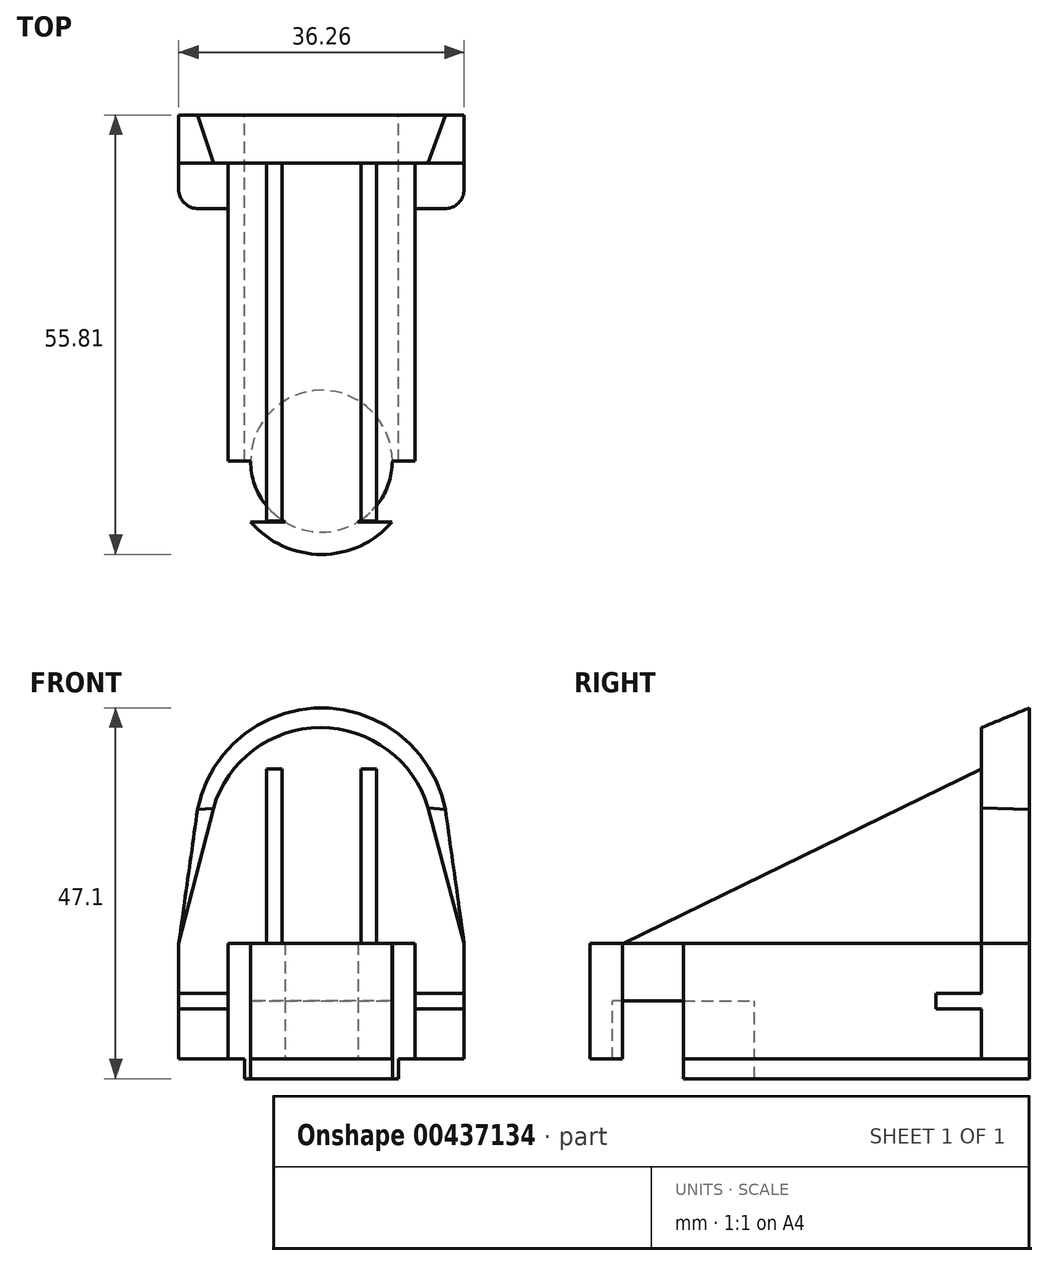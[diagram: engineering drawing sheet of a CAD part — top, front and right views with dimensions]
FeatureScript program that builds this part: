
annotation { "Feature Type Name" : "Feature", "Feature Type Description" : "" }
export const myFeature = defineFeature(function(context is Context, id is Id, definition is map)
    precondition{}
    {
        {
            var Q0;
            Q0=qCreatedBy(makeId("Front.planeOp"),FACE);
            var sketch = newSketch(context, id + "F0", { "sketchPlane" : qUnion([Q0])});
            skLineSegment(sketch, "E0.bottom", {"start": v(-18.13, 7.35) * mm, "end": v(18.13, 7.35) * mm});
            skLineSegment(sketch, "E0.top", {"start": v(-18.13, -7.35) * mm, "end": v(18.13, -7.35) * mm});
            skLineSegment(sketch, "E0.left", {"start": v(-18.13, 7.35) * mm, "end": v(-18.13, -7.35) * mm});
            skLineSegment(sketch, "E0.right", {"start": v(18.13, 7.35) * mm, "end": v(18.13, -7.35) * mm});
            skPoint(sketch, "E0.middle", {"position": v(0, 0) * mm});
            skLineSegment(sketch, "E1.bottom", {"start": v(-9.78, 7.35) * mm, "end": v(9.78, 7.35) * mm});
            skLineSegment(sketch, "E1.top", {"start": v(-9.78, -9.85) * mm, "end": v(9.78, -9.85) * mm});
            skLineSegment(sketch, "E1.left", {"start": v(-9.78, 7.35) * mm, "end": v(-9.78, -9.85) * mm});
            skLineSegment(sketch, "E1.right", {"start": v(9.78, 7.35) * mm, "end": v(9.78, -9.85) * mm});
            skPoint(sketch, "E1.middle", {"position": v(0, -1.25) * mm});
            skLineSegment(sketch, "E2.bottom", {"start": v(-11.87, 7.35) * mm, "end": v(11.87, 7.35) * mm});
            skLineSegment(sketch, "E2.top", {"start": v(-11.87, -7.35) * mm, "end": v(11.87, -7.35) * mm});
            skLineSegment(sketch, "E2.left", {"start": v(-11.87, 7.35) * mm, "end": v(-11.87, -7.35) * mm});
            skLineSegment(sketch, "E2.right", {"start": v(11.87, 7.35) * mm, "end": v(11.87, -7.35) * mm});
            skLineSegment(sketch, "E3", {"start": v(0, -9.85) * mm, "end": v(0, 37.25) * mm, "construction": true});
            skPoint(sketch, "E3.endSnap0", {"position": v(0, 7.35) * mm});
            skLineSegment(sketch, "E4", {"start": v(-18.13, 7.35) * mm, "end": v(-15.74, 24.38) * mm});
            skLineSegment(sketch, "E5.MirrorCS", {"start": v(18.13, 7.35) * mm, "end": v(15.74, 24.38) * mm});
            skArc(sketch, "E6", {"start": v(15.74, 24.38) * mm, "mid": v(0, 37.25) * mm, "end": v(-15.74, 24.38) * mm});
            skSolve(sketch);
        }
        {
            var Q0;
            Q0=qCreatedBy(makeId("Top.planeOp"),FACE);
            var sketch = newSketch(context, id + "F1", { "sketchPlane" : qUnion([Q0])});
            skLineSegment(sketch, "E7", {"start": v(0, 0) * mm, "end": v(0, -56) * mm, "construction": true});
            skLineSegment(sketch, "E8.bottom", {"start": v(-11.85, 0) * mm, "end": v(11.85, 0) * mm});
            skLineSegment(sketch, "E8.top", {"start": v(-11.85, -51.69) * mm, "end": v(11.85, -51.69) * mm});
            skLineSegment(sketch, "E8.left", {"start": v(-11.85, 0) * mm, "end": v(-11.85, -51.69) * mm});
            skLineSegment(sketch, "E8.right", {"start": v(11.85, 0) * mm, "end": v(11.85, -51.69) * mm});
            skPoint(sketch, "E8.middle", {"position": v(0, -25.84) * mm});
            skCircle(sketch, "E9", {"center": v(0, -43.96) * mm, "radius": 11.85 * mm});
            skLineSegment(sketch, "E10", {"start": v(-11.85, -43.96) * mm, "end": v(-11.85, -51.69) * mm});
            skLineSegment(sketch, "E11", {"start": v(11.85, -43.96) * mm, "end": v(11.85, -51.69) * mm});
            skCircle(sketch, "E12", {"center": v(0, -43.96) * mm, "radius": 9 * mm});
            skPoint(sketch, "E13.0", {"position": v(-9.78, 0) * mm});
            skPoint(sketch, "E14.0", {"position": v(9.78, 0) * mm});
            skLineSegment(sketch, "E15", {"start": v(-9.78, 0) * mm, "end": v(-9, -43.64) * mm});
            skLineSegment(sketch, "E16.bottom", {"start": v(-9, -43.64) * mm, "end": v(9, -43.64) * mm, "construction": true});
            skLineSegment(sketch, "E16.top", {"start": v(-9, -59.74) * mm, "end": v(9, -59.74) * mm, "construction": true});
            skLineSegment(sketch, "E16.left", {"start": v(-9, -43.64) * mm, "end": v(-9, -59.74) * mm, "construction": true});
            skLineSegment(sketch, "E16.right", {"start": v(9, -43.64) * mm, "end": v(9, -59.74) * mm, "construction": true});
            skPoint(sketch, "E16.middle", {"position": v(0, -51.69) * mm});
            skLineSegment(sketch, "E17", {"start": v(9.78, 0) * mm, "end": v(9, -43.64) * mm});
            skPoint(sketch, "E18.0", {"position": v(-18.13, 0) * mm});
            skPoint(sketch, "E19.0", {"position": v(18.13, 0) * mm});
            skLineSegment(sketch, "E20.bottom", {"start": v(-18.13, 0) * mm, "end": v(18.13, 0) * mm});
            skLineSegment(sketch, "E20.top", {"start": v(-18.13, -5.9) * mm, "end": v(18.13, -5.9) * mm});
            skLineSegment(sketch, "E20.left", {"start": v(-18.13, 0) * mm, "end": v(-18.13, -5.9) * mm});
            skLineSegment(sketch, "E20.right", {"start": v(18.13, 0) * mm, "end": v(18.13, -5.9) * mm});
            skPoint(sketch, "E21.oppositeSnap0", {"position": v(18.13, -2.95) * mm});
            skLineSegment(sketch, "E21.top", {"start": v(-15.63, -11.9) * mm, "end": v(15.63, -11.9) * mm});
            skLineSegment(sketch, "E21.left", {"start": v(-18.13, 0) * mm, "end": v(-18.13, -9.4) * mm});
            skLineSegment(sketch, "E21.right", {"start": v(18.13, 0) * mm, "end": v(18.13, -9.4) * mm});
            skPoint(sketch, "E22.visualSharp", {"position": v(-18.13, -11.9) * mm});
            skArc(sketch, "E22.filletArc", {"start": v(-18.13, -9.4) * mm, "mid": v(-17.4, -11.17) * mm, "end": v(-15.63, -11.9) * mm});
            skPoint(sketch, "E23.visualSharp", {"position": v(18.13, -11.9) * mm});
            skArc(sketch, "E23.filletArc", {"start": v(15.63, -11.9) * mm, "mid": v(17.4, -11.17) * mm, "end": v(18.13, -9.4) * mm});
            skPoint(sketch, "E24", {"position": v(0, -55.81) * mm});
            skLineSegment(sketch, "E25.top", {"start": v(-11.85, -58.25) * mm, "end": v(11.85, -58.25) * mm});
            skLineSegment(sketch, "E25.left", {"start": v(-11.85, -51.69) * mm, "end": v(-11.85, -58.25) * mm});
            skLineSegment(sketch, "E25.right", {"start": v(11.85, -51.69) * mm, "end": v(11.85, -58.25) * mm});
            skSolve(sketch);
        }
        {
            var Q0;
            Q0=qCreatedBy(makeId("Right.planeOp"),FACE);
            var sketch = newSketch(context, id + "F2", { "sketchPlane" : qUnion([Q0])});
            skPoint(sketch, "E26.0", {"position": v(0, -7.35) * mm});
            skPoint(sketch, "E27.0", {"position": v(0, -9.85) * mm});
            skPoint(sketch, "E28.0", {"position": v(0, 37.25) * mm});
            skPoint(sketch, "E29.0", {"position": v(0, 7.35) * mm});
            skLineSegment(sketch, "E30.bottom", {"start": v(0, -7.35) * mm, "end": v(-55.81, -7.35) * mm});
            skLineSegment(sketch, "E30.top", {"start": v(0, 7.35) * mm, "end": v(-55.81, 7.35) * mm});
            skLineSegment(sketch, "E30.left", {"start": v(0, -7.35) * mm, "end": v(0, 7.35) * mm});
            skLineSegment(sketch, "E30.right", {"start": v(-55.81, -7.35) * mm, "end": v(-55.81, 7.35) * mm});
            skPoint(sketch, "E31.0", {"position": v(-43.64, 0) * mm});
            skLineSegment(sketch, "E32.bottom", {"start": v(0, -9.85) * mm, "end": v(-43.64, -9.85) * mm});
            skLineSegment(sketch, "E32.top", {"start": v(0, 0) * mm, "end": v(-43.64, 0) * mm});
            skLineSegment(sketch, "E32.left", {"start": v(0, -9.85) * mm, "end": v(0, 0) * mm});
            skLineSegment(sketch, "E32.right", {"start": v(-43.64, -9.85) * mm, "end": v(-43.64, 0) * mm});
            skLineSegment(sketch, "E33", {"start": v(0, -7.35) * mm, "end": v(0, 29.5) * mm, "construction": true});
            skLineSegment(sketch, "E34", {"start": v(0, 29.5) * mm, "end": v(-10.09, 29.5) * mm, "construction": true});
            skLineSegment(sketch, "E35.bottom", {"start": v(0, 37.25) * mm, "end": v(-6.1, 37.25) * mm, "construction": true});
            skLineSegment(sketch, "E35.top", {"start": v(0, -7.35) * mm, "end": v(-6.1, -7.35) * mm, "construction": true});
            skLineSegment(sketch, "E35.left", {"start": v(0, 37.25) * mm, "end": v(0, -7.35) * mm, "construction": true});
            skLineSegment(sketch, "E35.right", {"start": v(-6.1, 37.25) * mm, "end": v(-6.1, -7.35) * mm, "construction": true});
            skLineSegment(sketch, "E36.bottom", {"start": v(0, 7.35) * mm, "end": v(-6.1, 7.35) * mm});
            skLineSegment(sketch, "E36.top", {"start": v(0, 37.25) * mm, "end": v(-6.1, 37.25) * mm});
            skLineSegment(sketch, "E36.left", {"start": v(0, 7.35) * mm, "end": v(0, 37.25) * mm});
            skLineSegment(sketch, "E36.right", {"start": v(-6.1, 7.35) * mm, "end": v(-6.1, 37.25) * mm});
            skLineSegment(sketch, "E37.top", {"start": v(0, 34.75) * mm, "end": v(-6.1, 34.75) * mm});
            skLineSegment(sketch, "E37.left", {"start": v(0, 7.35) * mm, "end": v(0, 34.75) * mm});
            skLineSegment(sketch, "E37.right", {"start": v(-6.1, 7.35) * mm, "end": v(-6.1, 34.75) * mm});
            skLineSegment(sketch, "E38", {"start": v(-6.1, 34.75) * mm, "end": v(0, 37.25) * mm});
            skLineSegment(sketch, "E39", {"start": v(-51.58, 0) * mm, "end": v(-51.58, 7.35) * mm, "construction": true});
            skLineSegment(sketch, "E40", {"start": v(-51.58, 7.35) * mm, "end": v(-6.1, 29.5) * mm});
            skLineSegment(sketch, "E41.0", {"start": v(0, 0) * mm, "end": v(-56, 0) * mm});
            skPoint(sketch, "E42.0", {"position": v(-55.81, 0) * mm});
            skSolve(sketch);
        }
        {
            var Q0;
            {var subQ0=sQuery(id+"F0.wireOp",EDGE,"E0.right");Q0=makeQuery(id+"F0.imprint","IMPRINT",FACE,{"disambiguationData":[TD([[makeQuery(id+"F0.imprint","IMPRINT",EDGE,{"derivedFrom":subQ0}),-1.0]])]});}
            var Q1;
            {var subQ5=sQuery(id+"F0.wireOp",EDGE,"E2.right");Q1=makeQuery(id+"F0.imprint","IMPRINT",FACE,{"disambiguationData":[TD([[makeQuery(id+"F0.imprint","IMPRINT",EDGE,{"derivedFrom":subQ5}),-1.0]])]});}
            var Q2;
            {var subQ0=sQuery(id+"F0.wireOp",EDGE,"E2.bottom");var subQ1=sQuery(id+"F0.wireOp",EDGE,"E1.left");var subQ2=makeQuery(id+"F0.imprint","INTERSECT",VERTEX,{"derivedFrom":[subQ1,subQ0]});Q2=makeQuery(id+"F0.imprint","IMPRINT",FACE,{"disambiguationData":[TD([[makeQuery(id+"F0.imprint","IMPRINT",EDGE,{"disambiguationData":[TD([[subQ2,-1.0]])],"derivedFrom":subQ1}),1.0]])]});}
            var Q3;
            {var subQ5=sQuery(id+"F0.wireOp",EDGE,"E2.left");Q3=makeQuery(id+"F0.imprint","IMPRINT",FACE,{"disambiguationData":[TD([[makeQuery(id+"F0.imprint","IMPRINT",EDGE,{"derivedFrom":subQ5}),1.0]])]});}
            var Q4;
            {var subQ0=sQuery(id+"F0.wireOp",EDGE,"E0.left");Q4=makeQuery(id+"F0.imprint","IMPRINT",FACE,{"disambiguationData":[TD([[makeQuery(id+"F0.imprint","IMPRINT",EDGE,{"derivedFrom":subQ0}),1.0]])]});}
            extrude(context, id + "F3", {"entities" : qUnion([Q0, Q1, Q2, Q3, Q4]), "depth" : 6.1 * mm});
        }
        {
            var Q0;
            {var subQ0=sQuery(id+"F0.wireOp",EDGE,"E2.bottom");var subQ1=sQuery(id+"F0.wireOp",EDGE,"E1.left");var subQ2=makeQuery(id+"F0.imprint","INTERSECT",VERTEX,{"derivedFrom":[subQ1,subQ0]});Q0=makeQuery(id+"F0.imprint","IMPRINT",FACE,{"disambiguationData":[TD([[makeQuery(id+"F0.imprint","IMPRINT",EDGE,{"disambiguationData":[TD([[subQ2,-1.0]])],"derivedFrom":subQ1}),1.0]])]});}
            var Q1;
            {var subQ5=sQuery(id+"F0.wireOp",EDGE,"E2.right");Q1=makeQuery(id+"F0.imprint","IMPRINT",FACE,{"disambiguationData":[TD([[makeQuery(id+"F0.imprint","IMPRINT",EDGE,{"derivedFrom":subQ5}),-1.0]])]});}
            var Q2;
            {var subQ5=sQuery(id+"F0.wireOp",EDGE,"E2.left");Q2=makeQuery(id+"F0.imprint","IMPRINT",FACE,{"disambiguationData":[TD([[makeQuery(id+"F0.imprint","IMPRINT",EDGE,{"derivedFrom":subQ5}),1.0]])]});}
            extrude(context, id + "F4", {"entities" : qUnion([Q0, Q1, Q2]), "operationType" : NewBodyOperationType.ADD, "depth" : 43.96 * mm});
        }
        {
            var Q0;
            {var subQ0=sQuery(id+"F1.wireOp",EDGE,"E9");var subQ5=makeQuery(id+"F1.imprint","INTERSECT",VERTEX,{"derivedFrom":[subQ0,sQuery(id+"F1.wireOp",EDGE,"E17")]});Q0=makeQuery(id+"F1.imprint","IMPRINT",FACE,{"disambiguationData":[TD([[makeQuery(id+"F1.imprint","IMPRINT",EDGE,{"disambiguationData":[TD([[subQ5,-1.0]])],"derivedFrom":subQ0}),1.0]])]});}
            var Q1;
            {var subQ0=sQuery(id+"F1.wireOp",EDGE,"E8.top");var subQ1=sQuery(id+"F1.wireOp",EDGE,"E12");var subQ2=makeQuery(id+"F1.imprint","INTERSECT",VERTEX,{"disambiguationData":[OD(0.0)],"derivedFrom":[subQ1,subQ0]});Q1=makeQuery(id+"F1.imprint","IMPRINT",FACE,{"disambiguationData":[TD([[makeQuery(id+"F1.imprint","IMPRINT",EDGE,{"disambiguationData":[TD([[subQ2,1.0]])],"derivedFrom":subQ1}),1.0]])]});}
            var Q2;
            {var subQ0=sQuery(id+"F1.wireOp",EDGE,"E8.top");var subQ1=sQuery(id+"F1.wireOp",EDGE,"E9");var subQ2=makeQuery(id+"F1.imprint","INTERSECT",VERTEX,{"disambiguationData":[OD(0.0)],"derivedFrom":[subQ1,subQ0]});Q2=makeQuery(id+"F1.imprint","IMPRINT",FACE,{"disambiguationData":[TD([[makeQuery(id+"F1.imprint","IMPRINT",EDGE,{"disambiguationData":[TD([[subQ2,-1.0]])],"derivedFrom":subQ1}),1.0]])]});}
            var Q3;
            {var subQ0=sQuery(id+"F1.wireOp",EDGE,"E8.top");var subQ1=sQuery(id+"F1.wireOp",EDGE,"E12");var subQ2=makeQuery(id+"F1.imprint","INTERSECT",VERTEX,{"disambiguationData":[OD(0.0)],"derivedFrom":[subQ1,subQ0]});Q3=makeQuery(id+"F1.imprint","IMPRINT",FACE,{"disambiguationData":[TD([[makeQuery(id+"F1.imprint","IMPRINT",EDGE,{"disambiguationData":[TD([[subQ2,-1.0]])],"derivedFrom":subQ1}),1.0]])]});}
            extrude(context, id + "F5", {"entities" : qUnion([Q0, Q1, Q2, Q3]), "operationType" : NewBodyOperationType.ADD, "depth" : 14.7 * mm, "symmetric" : true});
        }
        {
            var Q0;
            {var subQ0=sQuery(id+"F0.wireOp",EDGE,"E1.top");Q0=makeQuery(id+"F0.imprint","IMPRINT",FACE,{"disambiguationData":[TD([[makeQuery(id+"F0.imprint","IMPRINT",EDGE,{"derivedFrom":subQ0}),1.0]])]});}
            extrude(context, id + "F6", {"entities" : qUnion([Q0]), "operationType" : NewBodyOperationType.ADD, "depth" : 43.64 * mm});
        }
        {
            var Q0;
            {var subQ3=sQuery(id+"F1.wireOp",EDGE,"E22.filletArc");Q0=makeQuery(id+"F1.imprint","IMPRINT",FACE,{"disambiguationData":[TD([[makeQuery(id+"F1.imprint","IMPRINT",EDGE,{"derivedFrom":subQ3}),1.0]])]});}
            var Q1;
            {var subQ3=sQuery(id+"F1.wireOp",EDGE,"E23.filletArc");Q1=makeQuery(id+"F1.imprint","IMPRINT",FACE,{"disambiguationData":[TD([[makeQuery(id+"F1.imprint","IMPRINT",EDGE,{"derivedFrom":subQ3}),1.0]])]});}
            extrude(context, id + "F7", {"entities" : qUnion([Q0, Q1]), "operationType" : NewBodyOperationType.ADD, "depth" : 2 * mm, "symmetric" : true});
        }
        {
            var Q0;
            {var subQ0=sQuery(id+"F1.wireOp",EDGE,"E8.top");var subQ1=sQuery(id+"F1.wireOp",EDGE,"E12");var subQ2=makeQuery(id+"F1.imprint","INTERSECT",VERTEX,{"disambiguationData":[OD(0.0)],"derivedFrom":[subQ1,subQ0]});Q0=makeQuery(id+"F1.imprint","IMPRINT",FACE,{"disambiguationData":[TD([[makeQuery(id+"F1.imprint","IMPRINT",EDGE,{"disambiguationData":[TD([[subQ2,1.0]])],"derivedFrom":subQ1}),1.0]])]});}
            var Q1;
            {var subQ0=sQuery(id+"F1.wireOp",EDGE,"E8.top");var subQ1=sQuery(id+"F1.wireOp",EDGE,"E12");var subQ2=makeQuery(id+"F1.imprint","INTERSECT",VERTEX,{"disambiguationData":[OD(0.0)],"derivedFrom":[subQ1,subQ0]});Q1=makeQuery(id+"F1.imprint","IMPRINT",FACE,{"disambiguationData":[TD([[makeQuery(id+"F1.imprint","IMPRINT",EDGE,{"disambiguationData":[TD([[subQ2,-1.0]])],"derivedFrom":subQ1}),1.0]])]});}
            extrude(context, id + "F8", {"entities" : qUnion([Q0, Q1]), "operationType" : NewBodyOperationType.REMOVE, "oppositeDirection" : true, "depth" : 40 * mm});
        }
        {
            var Q0;
            Q0=makeQuery(id+"F1.imprint","IMPRINT",FACE,{"disambiguationData":[TD([[makeQuery(id+"F1.imprint","IMPRINT",EDGE,{"derivedFrom":sQuery(id+"F1.wireOp",EDGE,"E25.top")}),1.0]])]});
            var Q1;
            {var subQ0=sQuery(id+"F1.wireOp",EDGE,"E10");Q1=makeQuery(id+"F1.imprint","IMPRINT",FACE,{"disambiguationData":[TD([[makeQuery(id+"F1.imprint","IMPRINT",EDGE,{"derivedFrom":subQ0}),1.0]])]});}
            var Q2;
            {var subQ0=sQuery(id+"F1.wireOp",EDGE,"E11");Q2=makeQuery(id+"F1.imprint","IMPRINT",FACE,{"disambiguationData":[TD([[makeQuery(id+"F1.imprint","IMPRINT",EDGE,{"derivedFrom":subQ0}),-1.0]])]});}
            extrude(context, id + "F9", {"entities" : qUnion([Q0, Q1, Q2]), "operationType" : NewBodyOperationType.REMOVE, "endBound" : BoundingType.THROUGH_ALL, "oppositeDirection" : true, "depth" : 25 * mm});
        }
        {
            var Q0;
            Q0=makeQuery(id+"F1.imprint","IMPRINT",FACE,{"disambiguationData":[TD([[makeQuery(id+"F1.imprint","IMPRINT",EDGE,{"derivedFrom":sQuery(id+"F1.wireOp",EDGE,"E25.top")}),1.0]])]});
            var Q1;
            {var subQ0=sQuery(id+"F1.wireOp",EDGE,"E10");Q1=makeQuery(id+"F1.imprint","IMPRINT",FACE,{"disambiguationData":[TD([[makeQuery(id+"F1.imprint","IMPRINT",EDGE,{"derivedFrom":subQ0}),1.0]])]});}
            var Q2;
            {var subQ0=sQuery(id+"F1.wireOp",EDGE,"E11");Q2=makeQuery(id+"F1.imprint","IMPRINT",FACE,{"disambiguationData":[TD([[makeQuery(id+"F1.imprint","IMPRINT",EDGE,{"derivedFrom":subQ0}),-1.0]])]});}
            extrude(context, id + "F10", {"entities" : qUnion([Q0, Q1, Q2]), "operationType" : NewBodyOperationType.REMOVE, "endBound" : BoundingType.THROUGH_ALL, "depth" : 25 * mm});
        }
        {
            var Q0;
            {var subQ3=sQuery(id+"F2.wireOp",EDGE,"E40");Q0=makeQuery(id+"F2.imprint","IMPRINT",FACE,{"disambiguationData":[TD([[makeQuery(id+"F2.imprint","IMPRINT",EDGE,{"derivedFrom":subQ3}),-1.0]])]});}
            extrude(context, id + "F11", {"entities" : qUnion([Q0]), "operationType" : NewBodyOperationType.ADD, "depth" : 14 * mm, "symmetric" : true});
        }
        {
            var Q0;
            {var subQ0=sQuery(id+"F0.wireOp",EDGE,"E0.right");Q0=makeQuery(id+"F0.imprint","IMPRINT",FACE,{"disambiguationData":[TD([[makeQuery(id+"F0.imprint","IMPRINT",EDGE,{"derivedFrom":subQ0}),-1.0]])]});}
            var Q1;
            {var subQ0=sQuery(id+"F0.wireOp",EDGE,"E0.left");Q1=makeQuery(id+"F0.imprint","IMPRINT",FACE,{"disambiguationData":[TD([[makeQuery(id+"F0.imprint","IMPRINT",EDGE,{"derivedFrom":subQ0}),1.0]])]});}
            var Q2;
            {var subQ5=sQuery(id+"F0.wireOp",EDGE,"E2.left");Q2=makeQuery(id+"F0.imprint","IMPRINT",FACE,{"disambiguationData":[TD([[makeQuery(id+"F0.imprint","IMPRINT",EDGE,{"derivedFrom":subQ5}),1.0]])]});}
            var Q3;
            {var subQ0=sQuery(id+"F0.wireOp",EDGE,"E2.bottom");var subQ1=sQuery(id+"F0.wireOp",EDGE,"E1.left");var subQ2=makeQuery(id+"F0.imprint","INTERSECT",VERTEX,{"derivedFrom":[subQ1,subQ0]});Q3=makeQuery(id+"F0.imprint","IMPRINT",FACE,{"disambiguationData":[TD([[makeQuery(id+"F0.imprint","IMPRINT",EDGE,{"disambiguationData":[TD([[subQ2,-1.0]])],"derivedFrom":subQ1}),1.0]])]});}
            var Q4;
            {var subQ5=sQuery(id+"F0.wireOp",EDGE,"E2.right");Q4=makeQuery(id+"F0.imprint","IMPRINT",FACE,{"disambiguationData":[TD([[makeQuery(id+"F0.imprint","IMPRINT",EDGE,{"derivedFrom":subQ5}),-1.0]])]});}
            extrude(context, id + "F12", {"entities" : qUnion([Q0, Q1, Q2, Q3, Q4]), "operationType" : NewBodyOperationType.ADD, "depth" : 6.1 * mm});
        }
        {
            var Q0;
            {var subQ1=sQuery(id+"F0.wireOp",EDGE,"E2.top");var subQ2=sQuery(id+"F0.wireOp",EDGE,"E6");var subQ3=sQuery(id+"F0.wireOp",EDGE,"E5.MirrorCS");var subQ4=sQuery(id+"F0.wireOp",EDGE,"E4");var subQ5=sQuery(id+"F0.wireOp",EDGE,"E0.top");var subQ7=sQuery(id+"F0.wireOp",EDGE,"E1.left");var subQ8=sQuery(id+"F0.wireOp",EDGE,"E0.left");var subQ11=sQuery(id+"F0.wireOp",EDGE,"E1.right");var subQ12=sQuery(id+"F0.wireOp",EDGE,"E0.right");Q0=makeQuery(id+"F4.boolean.opBoolean","SPLIT",FACE,{"disambiguationData":[TD([makeQuery(id+"F3.opExtrude","SWEPT_FACE",FACE,{"disambiguationData":[OSD([subQ8])]})])],"derivedFrom":makeQuery(id+"F3.opExtrude","CAP_FACE",FACE,{"disambiguationData":[OSD([subQ5,subQ8,subQ12,sQuery(id+"F0.wireOp",EDGE,"E1.top"),subQ7,subQ11,subQ1,subQ4,subQ3,subQ2])],"isStart":false})});}
            var sketch = newSketch(context, id + "F13", { "sketchPlane" : qUnion([Q0])});
            skPoint(sketch, "E43.0", {"position": v(18.13, 7.35) * mm});
            skPoint(sketch, "E44.0", {"position": v(0, 7.35) * mm});
            skPoint(sketch, "E45.0", {"position": v(-18.13, 7.35) * mm});
            skPoint(sketch, "E46.0", {"position": v(0, 34.75) * mm});
            skPoint(sketch, "E47.0", {"position": v(0, 37.25) * mm});
            skLineSegment(sketch, "E48.0", {"start": v(-18.13, 7.35) * mm, "end": v(18.13, 7.35) * mm});
            skLineSegment(sketch, "E49.0", {"start": v(0, 7.35) * mm, "end": v(0, 34.75) * mm});
            skLineSegment(sketch, "E50.0", {"start": v(18.13, 7.35) * mm, "end": v(13.53, 24.57) * mm});
            skLineSegment(sketch, "E51.0", {"start": v(-18.13, 7.35) * mm, "end": v(-13.73, 24.49) * mm});
            skLineSegment(sketch, "E52", {"start": v(13.53, 24.57) * mm, "end": v(-13.73, 24.49) * mm});
            skArc(sketch, "E53", {"start": v(13.53, 24.57) * mm, "mid": v(-0.13, 34.75) * mm, "end": v(-13.73, 24.49) * mm});
            skSolve(sketch);
        }
        {
            var Q0;
            {var subQ7=sQuery(id+"F0.wireOp",EDGE,"E4");Q0=makeQuery(id+"F0.imprint","IMPRINT",FACE,{"disambiguationData":[TD([[makeQuery(id+"F0.imprint","IMPRINT",EDGE,{"derivedFrom":subQ7}),-1.0]])]});}
            extrude(context, id + "F14", {"entities" : qUnion([Q0]), "operationType" : NewBodyOperationType.ADD, "depth" : 0 * mm});
        }
        {
            var Q0;
            {var subQ5=sQuery(id+"F13.wireOp",EDGE,"E51.0");Q0=makeQuery(id+"F13.imprint","IMPRINT",FACE,{"disambiguationData":[TD([[makeQuery(id+"F13.imprint","IMPRINT",EDGE,{"derivedFrom":subQ5}),-1.0]])]});}
            var Q1;
            {var subQ0=sQuery(id+"F13.wireOp",EDGE,"E50.0");Q1=makeQuery(id+"F13.imprint","IMPRINT",FACE,{"disambiguationData":[TD([[makeQuery(id+"F13.imprint","IMPRINT",EDGE,{"derivedFrom":subQ0}),1.0]])]});}
            var Q2;
            {var subQ0=sQuery(id+"F13.wireOp",EDGE,"E53");var subQ1=sQuery(id+"F13.wireOp",EDGE,"E49.0");var subQ2=makeQuery(id+"F13.imprint","INTERSECT",VERTEX,{"derivedFrom":[subQ1,subQ0]});Q2=makeQuery(id+"F13.imprint","IMPRINT",FACE,{"disambiguationData":[TD([[makeQuery(id+"F13.imprint","IMPRINT",EDGE,{"disambiguationData":[TD([[subQ2,1.0]])],"derivedFrom":subQ1}),-1.0]])]});}
            var Q3;
            {var subQ0=sQuery(id+"F13.wireOp",EDGE,"E53");var subQ1=sQuery(id+"F13.wireOp",EDGE,"E49.0");var subQ2=makeQuery(id+"F13.imprint","INTERSECT",VERTEX,{"derivedFrom":[subQ1,subQ0]});Q3=makeQuery(id+"F13.imprint","IMPRINT",FACE,{"disambiguationData":[TD([[makeQuery(id+"F13.imprint","IMPRINT",EDGE,{"disambiguationData":[TD([[subQ2,1.0]])],"derivedFrom":subQ1}),1.0]])]});}
            extrude(context, id + "F15", {"entities" : qUnion([Q0, Q1, Q2, Q3]), "operationType" : NewBodyOperationType.ADD, "oppositeDirection" : true, "depth" : 0 * mm});
        }
        {
            var Q1;
            {var subQ7=sQuery(id+"F0.wireOp",EDGE,"E4");Q1=makeQuery(id+"F0.imprint","IMPRINT",FACE,{"disambiguationData":[TD([[makeQuery(id+"F0.imprint","IMPRINT",EDGE,{"derivedFrom":subQ7}),-1.0]])]});}
            var Q2;
            Q2=makeQuery(id+"F15.opExtrude","CAP_FACE",FACE,{"disambiguationData":[OSD([sQuery(id+"F13.wireOp",EDGE,"E48.0"),sQuery(id+"F13.wireOp",EDGE,"E50.0"),sQuery(id+"F13.wireOp",EDGE,"E51.0"),sQuery(id+"F13.wireOp",EDGE,"E53")])],"isStart":false});
            loft(context, id + "F16", {"operationType" : NewBodyOperationType.ADD, "sheetProfilesArray" : [{ "sheetProfileEntities" : qUnion([Q1]) }, { "sheetProfileEntities" : qUnion([Q2]) }]});
        }
        {
            var Q0;
            {var subQ3=sQuery(id+"F2.wireOp",EDGE,"E40");Q0=makeQuery(id+"F2.imprint","IMPRINT",FACE,{"disambiguationData":[TD([[makeQuery(id+"F2.imprint","IMPRINT",EDGE,{"derivedFrom":subQ3}),-1.0]])]});}
            extrude(context, id + "F17", {"entities" : qUnion([Q0]), "operationType" : NewBodyOperationType.REMOVE, "oppositeDirection" : true, "depth" : 10 * mm, "symmetric" : true});
        }
    });
